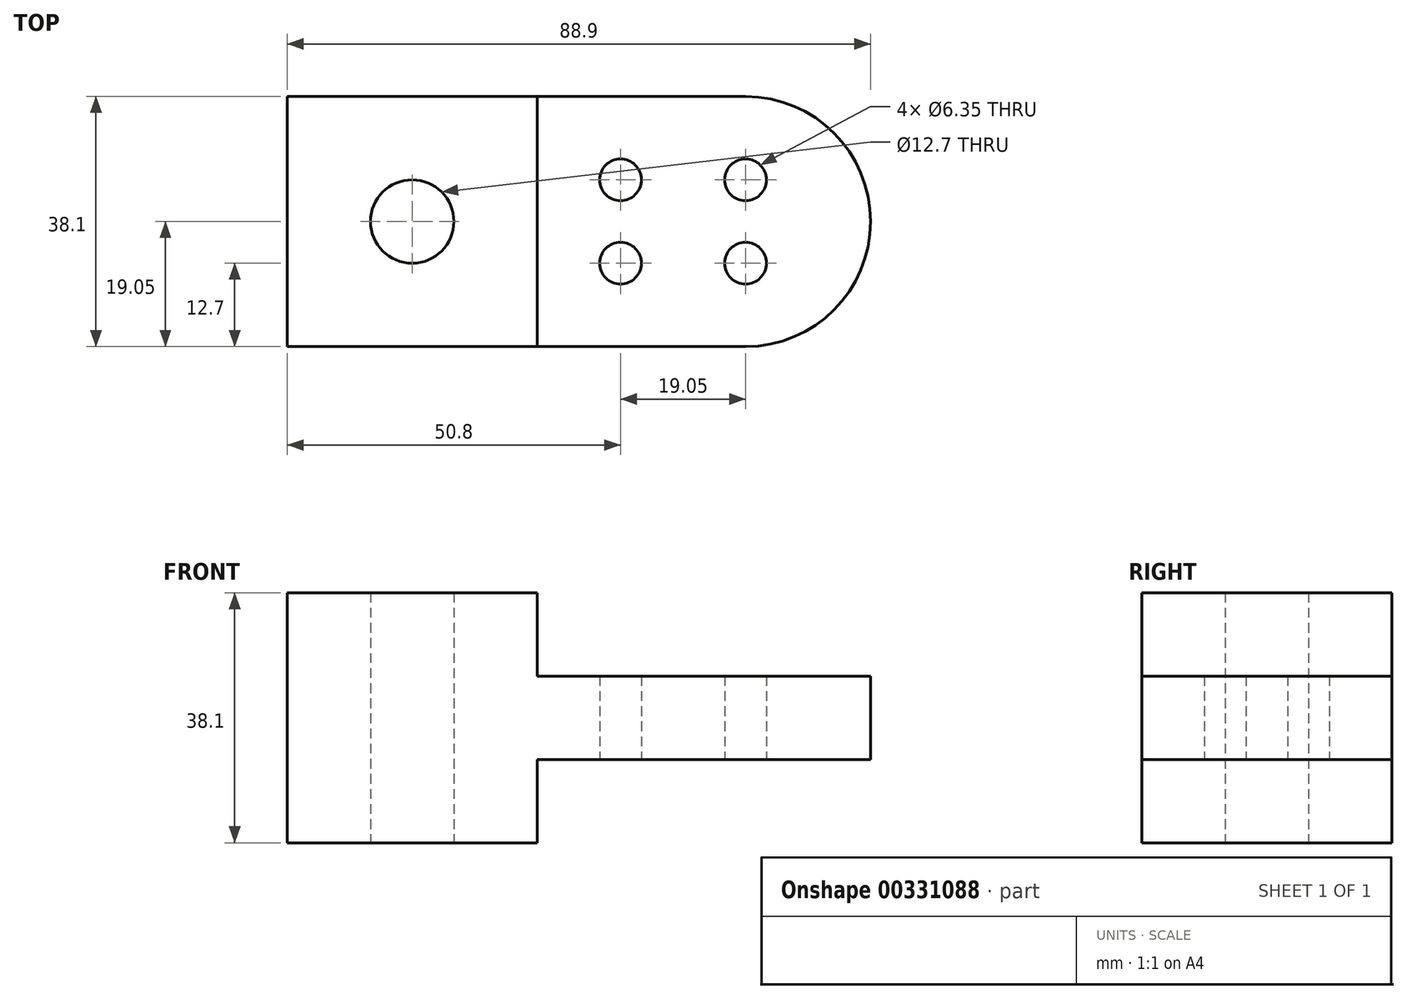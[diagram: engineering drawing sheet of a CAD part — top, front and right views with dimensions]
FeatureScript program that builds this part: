
annotation { "Feature Type Name" : "Feature", "Feature Type Description" : "" }
export const myFeature = defineFeature(function(context is Context, id is Id, definition is map)
    precondition{}
    {
        {
            var Q0;
            Q0=qCreatedBy(makeId("Top.planeOp"),FACE);
            var sketch = newSketch(context, id + "F0", { "sketchPlane" : qUnion([Q0])});
            skLineSegment(sketch, "E0.bottom", {"start": v(0, 0) * mm, "end": v(38.1, 0) * mm});
            skLineSegment(sketch, "E0.top", {"start": v(0, 38.1) * mm, "end": v(38.1, 38.1) * mm});
            skLineSegment(sketch, "E0.left", {"start": v(0, 0) * mm, "end": v(0, 38.1) * mm});
            skLineSegment(sketch, "E0.right", {"start": v(38.1, 0) * mm, "end": v(38.1, 38.1) * mm});
            skLineSegment(sketch, "E1", {"start": v(38.1, 38.1) * mm, "end": v(69.85, 38.1) * mm});
            skLineSegment(sketch, "E2", {"start": v(38.1, 0) * mm, "end": v(69.85, 0) * mm});
            skArc(sketch, "E3", {"start": v(69.85, 0) * mm, "mid": v(88.9, 19.05) * mm, "end": v(69.85, 38.1) * mm});
            skLineSegment(sketch, "E4", {"start": v(50.8, 38.1) * mm, "end": v(50.8, 0) * mm, "construction": true});
            skLineSegment(sketch, "E5", {"start": v(69.85, 38.1) * mm, "end": v(69.85, 0) * mm, "construction": true});
            skLineSegment(sketch, "E6", {"start": v(38.1, 25.4) * mm, "end": v(87.81, 25.4) * mm, "construction": true});
            skLineSegment(sketch, "E7", {"start": v(38.1, 12.7) * mm, "end": v(87.81, 12.7) * mm, "construction": true});
            skCircle(sketch, "E8", {"center": v(19.05, 19.05) * mm, "radius": 6.35 * mm});
            skPoint(sketch, "E8.centerSnap0", {"position": v(0, 19.05) * mm});
            skPoint(sketch, "E8.centerSnap1", {"position": v(19.05, 38.1) * mm});
            skCircle(sketch, "E9", {"center": v(50.8, 25.4) * mm, "radius": 3.18 * mm});
            skCircle(sketch, "E10", {"center": v(69.85, 25.4) * mm, "radius": 3.18 * mm});
            skCircle(sketch, "E11", {"center": v(50.8, 12.7) * mm, "radius": 3.18 * mm});
            skCircle(sketch, "E12", {"center": v(69.85, 12.7) * mm, "radius": 3.18 * mm});
            skSolve(sketch);
        }
        {
            var Q0;
            Q0=makeQuery(id+"F0.imprint","IMPRINT",FACE,{"disambiguationData":[TD([[makeQuery(id+"F0.imprint","IMPRINT",EDGE,{"derivedFrom":sQuery(id+"F0.wireOp",EDGE,"E0.bottom")}),1.0]])]});
            extrude(context, id + "F1", {"entities" : qUnion([Q0]), "depth" : 38.1 * mm, "symmetric" : true});
        }
        {
            var Q0;
            Q0=makeQuery(id+"F0.imprint","IMPRINT",FACE,{"disambiguationData":[TD([[makeQuery(id+"F0.imprint","IMPRINT",EDGE,{"derivedFrom":sQuery(id+"F0.wireOp",EDGE,"E0.right")}),-1.0]])]});
            extrude(context, id + "F2", {"entities" : qUnion([Q0]), "operationType" : NewBodyOperationType.ADD, "depth" : 12.7 * mm, "symmetric" : true});
        }
    });
